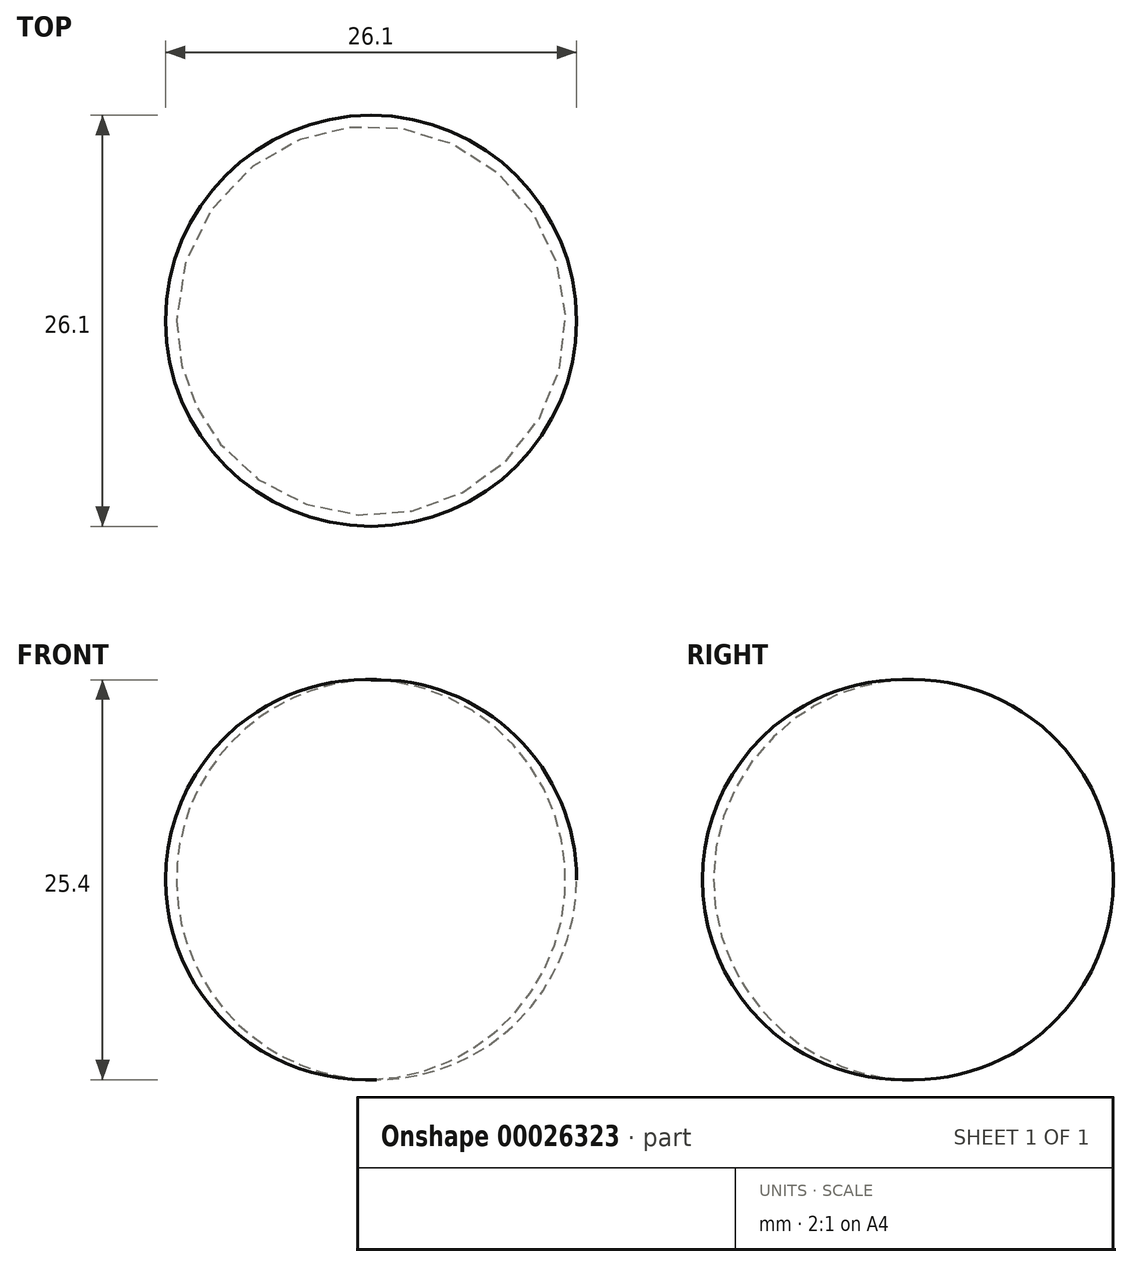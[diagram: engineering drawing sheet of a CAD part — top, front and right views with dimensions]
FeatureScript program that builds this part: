
annotation { "Feature Type Name" : "Feature", "Feature Type Description" : "" }
export const myFeature = defineFeature(function(context is Context, id is Id, definition is map)
    precondition{}
    {
        {
            var Q0;
            Q0=qCreatedBy(makeId("Front.planeOp"),FACE);
            var sketch = newSketch(context, id + "F0", { "sketchPlane" : qUnion([Q0])});
            skPoint(sketch, "E0", {"position": v(0, 12.7) * mm});
            skPoint(sketch, "E1", {"position": v(0, -12.7) * mm});
            skArc(sketch, "E2", {"start": v(0, -12.7) * mm, "mid": v(13.05, 0) * mm, "end": v(0, 12.7) * mm});
            skLineSegment(sketch, "E3", {"start": v(0, 12.7) * mm, "end": v(0, -12.7) * mm});
            skSolve(sketch);
        }
        {
            var Q0;
            Q0=makeQuery(id+"F0.imprint","IMPRINT",FACE,{"disambiguationData":[TD([[makeQuery(id+"F0.imprint","IMPRINT",EDGE,{"derivedFrom":sQuery(id+"F0.wireOp",EDGE,"E2")}),1.0]])]});
            var Q1;
            Q1=sQuery(id+"F0.wireOp",EDGE,"E3");
            revolve(context, id + "F1", {"entities" : qUnion([Q0]), "axis" : qUnion([Q1]), "revolveType" : RevolveType.FULL});
        }
    });
